# Revit family: FU_Inspec_Cinema_8-1
name_source: partatom
category: Furniture
units: mm (PartAtom-declared; Revit-internal decimal feet)

## family parameters
Always vertical = Yes
Cut with Voids When Loaded = No
OmniClass Number = 23.40.20.00
OmniClass Title = General Furniture and Specialties
Room Calculation Point = No
Shared = No
Work Plane-Based = No

## types (2) — shared parameters
Assembly Code = E2020
Description = Upholstered footstool with wood base in molded highly resilient polyurethane foam and powder coated or chromium plated steel tubular legs.
Keynote = 46.B
Manufacturer = Inspec
Model = Cinema 8.1
URL = https://inspecfurniture.com
zero-valued in all types: Default Elevation

## per-type parameters (varying)
| type | Frame Material | Seat Material |
| Fabric/Paint | Metal - White - Matte | Fabric - Green |
| Leather/Chrome | Metal - Chrome - Polished | Leather - Rustical - Black |

## geometry (parser evidence)
native form markers: Blend x10, Sweep x3
no freeform markers — native parametric forms only
